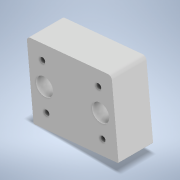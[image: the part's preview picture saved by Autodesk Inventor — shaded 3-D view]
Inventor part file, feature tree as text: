
AUTODESK INVENTOR PART (.ipt)
format: ipt  version: 2020 (Build 240168000, 168)  size: 131,072 bytes
history: native  units: in
note: dims shown in document units (in); Inventor stores cm internally (conversion verified against a paired STEP export)
features: other x3, extrude x1, sketch x1, reference x1
ambient origin geometry x8: Origin, YZ Plane, XZ Plane, XY Plane, X Axis, Y Axis, Z Axis, Center Point
bodies: Solid1 (feature_tree)
feature tree (6):
  extrude  "Extrusion1"  Depth=0.75in
  sketch  "Sketch1"  dims[d0=0.1181in d1=0.1181in d3=0.1181in d4=0.75in d5=0.0in d6=0.1181in]
  reference  "Reference1"
  other  "<userpath>\Desktop\PnP Machine\PnP Machine.iam"
  other  "PnP Machine.iam"
  other  "Head Back:1"
